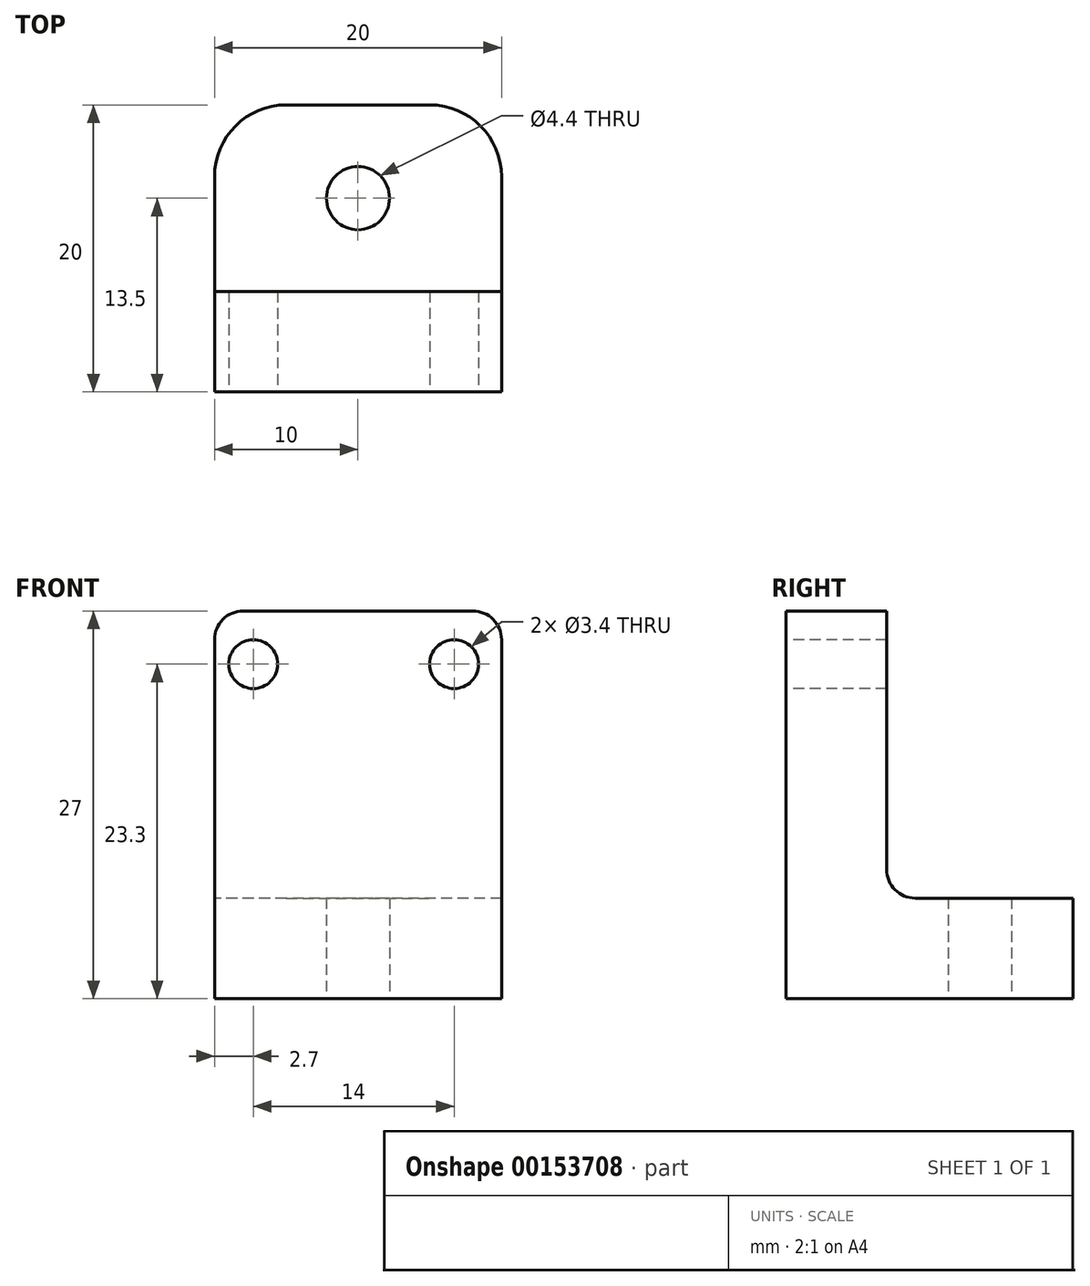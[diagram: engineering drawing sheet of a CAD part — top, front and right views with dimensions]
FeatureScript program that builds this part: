
annotation { "Feature Type Name" : "Feature", "Feature Type Description" : "" }
export const myFeature = defineFeature(function(context is Context, id is Id, definition is map)
    precondition{}
    {
        {
            var Q0;
            Q0=qCreatedBy(makeId("Top.planeOp"),FACE);
            var sketch = newSketch(context, id + "F0", { "sketchPlane" : qUnion([Q0])});
            skLineSegment(sketch, "E0.bottom", {"start": v(0, 0) * mm, "end": v(20, 0) * mm});
            skLineSegment(sketch, "E0.top", {"start": v(0, 20) * mm, "end": v(20, 20) * mm});
            skLineSegment(sketch, "E0.left", {"start": v(0, 0) * mm, "end": v(0, 20) * mm});
            skLineSegment(sketch, "E0.right", {"start": v(20, 0) * mm, "end": v(20, 20) * mm});
            skCircle(sketch, "E1", {"center": v(10, 13.5) * mm, "radius": 2.2 * mm});
            skPoint(sketch, "E1.centerSnap0", {"position": v(20, 13.5) * mm});
            skPoint(sketch, "E1.centerSnap1", {"position": v(10, 20) * mm});
            skSolve(sketch);
        }
        {
            var Q0;
            Q0=makeQuery(id+"F0.imprint","IMPRINT",FACE,{"disambiguationData":[TD([[makeQuery(id+"F0.imprint","IMPRINT",EDGE,{"derivedFrom":sQuery(id+"F0.wireOp",EDGE,"E0.bottom")}),1.0]])]});
            extrude(context, id + "F1", {"entities" : qUnion([Q0]), "depth" : 7 * mm});
        }
        {
            var Q0;
            Q0=qCreatedBy(makeId("Top.planeOp"),FACE);
            var sketch = newSketch(context, id + "F2", { "sketchPlane" : qUnion([Q0])});
            skLineSegment(sketch, "E2.bottom", {"start": v(0, 0) * mm, "end": v(20, 0) * mm});
            skLineSegment(sketch, "E2.top", {"start": v(0, 7) * mm, "end": v(20, 7) * mm});
            skLineSegment(sketch, "E2.left", {"start": v(0, 0) * mm, "end": v(0, 7) * mm});
            skLineSegment(sketch, "E2.right", {"start": v(20, 0) * mm, "end": v(20, 7) * mm});
            skSolve(sketch);
        }
        {
            var Q0;
            Q0 = qSketchRegion(id + "F2", true);
            extrude(context, id + "F3", {"entities" : qUnion([Q0]), "operationType" : NewBodyOperationType.ADD, "depth" : 27 * mm});
        }
        {
            var Q0;
            Q0=makeQuery(id+"F3.boolean.opBoolean","MERGE",FACE,{"derivedFrom":[makeQuery(id+"F1.opExtrude","SWEPT_FACE",FACE,{"disambiguationData":[OSD([sQuery(id+"F0.wireOp",EDGE,"E0.bottom")])]}),makeQuery(id+"F3.opExtrude","SWEPT_FACE",FACE,{"disambiguationData":[OSD([sQuery(id+"F2.wireOp",EDGE,"E2.bottom")])]})]});
            var sketch = newSketch(context, id + "F4", { "sketchPlane" : qUnion([Q0])});
            skCircle(sketch, "E3", {"center": v(16.7, 23.3) * mm, "radius": 1.7 * mm});
            skCircle(sketch, "E4", {"center": v(2.7, 23.3) * mm, "radius": 1.7 * mm});
            skSolve(sketch);
        }
        {
            var Q0;
            Q0=makeQuery(id+"F4.imprint","IMPRINT",FACE,{"disambiguationData":[TD([[makeQuery(id+"F4.imprint","IMPRINT",EDGE,{"derivedFrom":sQuery(id+"F4.wireOp",EDGE,"E4")}),1.0]])]});
            var Q1;
            Q1=makeQuery(id+"F4.imprint","IMPRINT",FACE,{"disambiguationData":[TD([[makeQuery(id+"F4.imprint","IMPRINT",EDGE,{"derivedFrom":sQuery(id+"F4.wireOp",EDGE,"E3")}),1.0]])]});
            extrude(context, id + "F5", {"entities" : qUnion([Q0, Q1]), "operationType" : NewBodyOperationType.REMOVE, "endBound" : BoundingType.UP_TO_NEXT, "oppositeDirection" : true, "depth" : 25 * mm});
        }
        {
            var Q0;
            Q0=makeQuery(id+"F1.opExtrude","SWEPT_EDGE",EDGE,{"disambiguationData":[OSD([sQuery(id+"F0.wireOp",EDGE,"E0.top"),sQuery(id+"F0.wireOp",EDGE,"E0.left")])]});
            var Q1;
            Q1=makeQuery(id+"F1.opExtrude","SWEPT_EDGE",EDGE,{"disambiguationData":[OSD([sQuery(id+"F0.wireOp",EDGE,"E0.top"),sQuery(id+"F0.wireOp",EDGE,"E0.right")])]});
            fillet(context, id + "F6", {"entities" : qUnion([Q0, Q1]), "radius" : 5 * mm, "tangentPropagation" : true, "allowEdgeOverflow" : false});
        }
        {
            var Q0;
            Q0=makeQuery(id+"F3.opExtrude","CAP_EDGE",EDGE,{"disambiguationData":[OSD([sQuery(id+"F2.wireOp",EDGE,"E2.left")])],"isStart":false});
            var Q1;
            Q1=makeQuery(id+"F3.opExtrude","CAP_EDGE",EDGE,{"disambiguationData":[OSD([sQuery(id+"F2.wireOp",EDGE,"E2.right")])],"isStart":false});
            var Q2;
            Q2=makeQuery(id+"F3.boolean.opBoolean","INTERSECT",EDGE,{"derivedFrom":[makeQuery(id+"F1.opExtrude","CAP_FACE",FACE,{"disambiguationData":[OSD([sQuery(id+"F0.wireOp",EDGE,"E0.bottom"),sQuery(id+"F0.wireOp",EDGE,"E0.top"),sQuery(id+"F0.wireOp",EDGE,"E0.left"),sQuery(id+"F0.wireOp",EDGE,"E0.right"),sQuery(id+"F0.wireOp",EDGE,"E1")])],"isStart":false}),makeQuery(id+"F3.opExtrude","SWEPT_FACE",FACE,{"disambiguationData":[OSD([sQuery(id+"F2.wireOp",EDGE,"E2.top")])]})]});
            fillet(context, id + "F7", {"entities" : qUnion([Q0, Q1, Q2]), "radius" : 2 * mm, "tangentPropagation" : true, "allowEdgeOverflow" : false});
        }
    });
